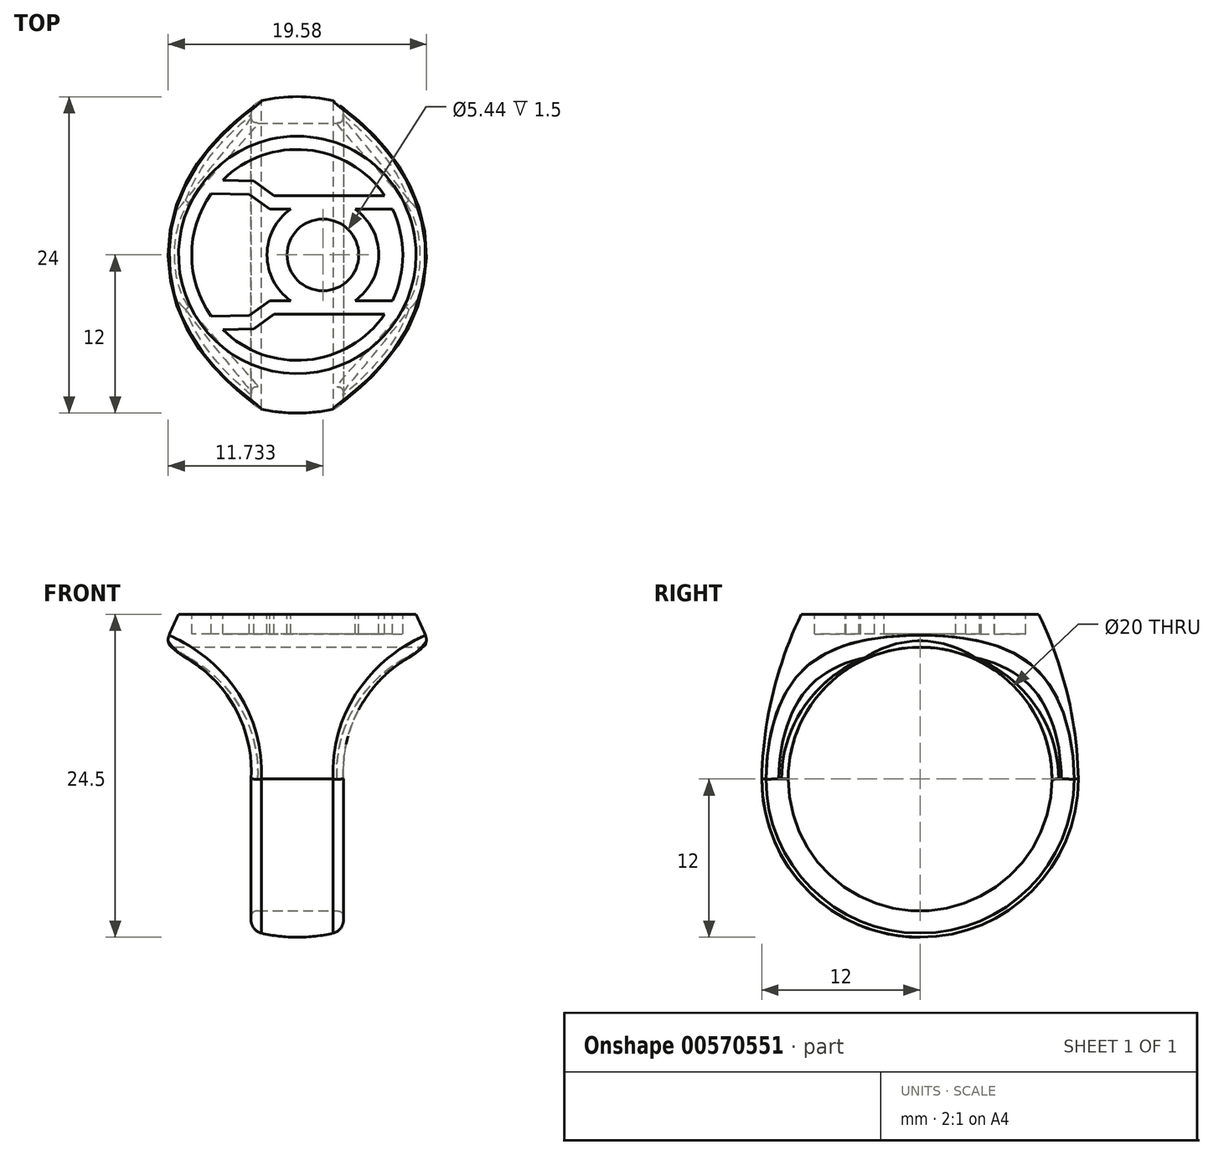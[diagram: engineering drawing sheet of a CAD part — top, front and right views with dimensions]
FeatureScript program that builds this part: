
annotation { "Feature Type Name" : "Feature", "Feature Type Description" : "" }
export const myFeature = defineFeature(function(context is Context, id is Id, definition is map)
    precondition{}
    {
        {
            var Q0;
            Q0=qCreatedBy(makeId("Right.planeOp"),FACE);
            var sketch = newSketch(context, id + "F0", { "sketchPlane" : qUnion([Q0])});
            skLineSegment(sketch, "E0", {"start": v(0, 0) * mm, "end": v(0, -24.5) * mm});
            skLineSegment(sketch, "E1", {"start": v(0, 0) * mm, "end": v(-9, 0) * mm});
            skArc(sketch, "E2", {"start": v(-12, -12.5) * mm, "mid": v(-8.49, -20.99) * mm, "end": v(0, -24.5) * mm});
            skLineSegment(sketch, "E3", {"start": v(0, -12.5) * mm, "end": v(-12, -12.5) * mm, "construction": true});
            skArc(sketch, "E4", {"start": v(-9, 0) * mm, "mid": v(-11.18, -6.09) * mm, "end": v(-12, -12.5) * mm});
            skSolve(sketch);
        }
        {
            var Q0;
            Q0=makeQuery(id+"F0.imprint","IMPRINT",FACE,{"disambiguationData":[TD([[makeQuery(id+"F0.imprint","IMPRINT",EDGE,{"derivedFrom":sQuery(id+"F0.wireOp",EDGE,"E0")}),-1.0]])]});
            var Q1;
            Q1=sQuery(id+"F0.wireOp",EDGE,"E0");
            revolve(context, id + "F1", {"entities" : qUnion([Q0]), "axis" : qUnion([Q1]), "revolveType" : RevolveType.FULL});
        }
        {
            var Q0;
            Q0=qCreatedBy(makeId("Right.planeOp"),FACE);
            var sketch = newSketch(context, id + "F2", { "sketchPlane" : qUnion([Q0])});
            skCircle(sketch, "E5", {"center": v(0, -12.5) * mm, "radius": 10 * mm});
            skSolve(sketch);
        }
        {
            var Q0;
            Q0=qSketchRegion(id+"F2",true);
            extrude(context, id + "F3", {"entities" : qUnion([Q0]), "operationType" : NewBodyOperationType.REMOVE, "oppositeDirection" : true, "depth" : 25 * mm, "offsetDistance" : 25 * mm, "symmetric" : true});
        }
        {
            var Q0;
            Q0=qCreatedBy(makeId("Front.planeOp"),FACE);
            var sketch = newSketch(context, id + "F4", { "sketchPlane" : qUnion([Q0])});
            skLineSegment(sketch, "E6", {"start": v(3.5, -26.5) * mm, "end": v(3.5, -12.5) * mm});
            skArc(sketch, "E7", {"start": v(10.15, -2.5) * mm, "mid": v(5.16, -6.39) * mm, "end": v(3.5, -12.5) * mm});
            skLineSegment(sketch, "E8", {"start": v(10.15, -2.5) * mm, "end": v(11.65, -2.5) * mm});
            skLineSegment(sketch, "E9", {"start": v(11.65, -2.5) * mm, "end": v(11.65, -26.5) * mm});
            skLineSegment(sketch, "E10", {"start": v(11.65, -26.5) * mm, "end": v(3.5, -26.5) * mm});
            skPoint(sketch, "E11.start.orphan", {"position": v(0, -24.5) * mm});
            skLineSegment(sketch, "E12", {"start": v(0, 0) * mm, "end": v(0, -24.5) * mm, "construction": true});
            skLineSegment(sketch, "E13.MirrorCS", {"start": v(-3.5, -26.5) * mm, "end": v(-3.5, -12.5) * mm});
            skArc(sketch, "E14.MirrorCS", {"start": v(-10.15, -2.5) * mm, "mid": v(-5.16, -6.39) * mm, "end": v(-3.5, -12.5) * mm});
            skLineSegment(sketch, "E15.MirrorCS", {"start": v(-11.65, -2.5) * mm, "end": v(-11.65, -26.5) * mm});
            skLineSegment(sketch, "E16.MirrorCS", {"start": v(-11.65, -26.5) * mm, "end": v(-3.5, -26.5) * mm});
            skLineSegment(sketch, "E17.MirrorCS", {"start": v(-10.15, -2.5) * mm, "end": v(-11.65, -2.5) * mm});
            skSolve(sketch);
        }
        {
            var Q0;
            Q0=qSketchRegion(id+"F4",true);
            extrude(context, id + "F5", {"entities" : qUnion([Q0]), "operationType" : NewBodyOperationType.REMOVE, "depth" : 25 * mm, "offsetDistance" : 25 * mm, "symmetric" : true});
        }
        {
            var Q0;
            Q0=makeQuery(id+"F1.opRevolve","SWEPT_FACE",FACE,{"disambiguationData":[OSD([sQuery(id+"F0.wireOp",EDGE,"E1")])]});
            var sketch = newSketch(context, id + "F6", { "sketchPlane" : qUnion([Q0])});
            skArc(sketch, "E18", {"start": v(-6.52, 4.64) * mm, "mid": v(-8, 0) * mm, "end": v(-6.52, -4.64) * mm});
            skLineSegment(sketch, "E19", {"start": v(-8, 0) * mm, "end": v(8, 0) * mm, "construction": true});
            skArc(sketch, "E20", {"start": v(4.66, 0) * mm, "mid": v(1.94, 2.72) * mm, "end": v(-0.77, 0) * mm});
            skArc(sketch, "E21", {"start": v(-0.5, 3.46) * mm, "mid": v(-1.82, 1.95) * mm, "end": v(-2.3, 0) * mm});
            skLineSegment(sketch, "E22", {"start": v(6.61, 4.5) * mm, "end": v(-1.75, 4.5) * mm});
            skLineSegment(sketch, "E23", {"start": v(-1.75, 4.5) * mm, "end": v(-3.3, 5.61) * mm});
            skLineSegment(sketch, "E24", {"start": v(-3.3, 5.61) * mm, "end": v(-5.65, 5.66) * mm});
            skLineSegment(sketch, "E25", {"start": v(7.21, 3.46) * mm, "end": v(4.38, 3.46) * mm});
            skLineSegment(sketch, "E26", {"start": v(-2.09, 3.46) * mm, "end": v(-3.64, 4.58) * mm});
            skLineSegment(sketch, "E27", {"start": v(-3.64, 4.58) * mm, "end": v(-6.52, 4.64) * mm});
            skLineSegment(sketch, "E28.trimOffspring", {"start": v(-0.5, 3.46) * mm, "end": v(-2.09, 3.46) * mm});
            skArc(sketch, "E29.trimOffspring", {"start": v(6.18, 0) * mm, "mid": v(5.7, 1.95) * mm, "end": v(4.38, 3.46) * mm});
            skArc(sketch, "E30.trimOffspring", {"start": v(6.61, 4.5) * mm, "mid": v(0.75, 7.96) * mm, "end": v(-5.65, 5.66) * mm});
            skLineSegment(sketch, "E31.MirrorCS", {"start": v(7.21, -3.46) * mm, "end": v(4.38, -3.46) * mm});
            skArc(sketch, "E32.MirrorCS", {"start": v(6.18, 0) * mm, "mid": v(5.7, -1.95) * mm, "end": v(4.38, -3.46) * mm});
            skArc(sketch, "E33.MirrorCS", {"start": v(4.66, 0) * mm, "mid": v(1.94, -2.72) * mm, "end": v(-0.77, 0) * mm});
            skArc(sketch, "E34.MirrorCS", {"start": v(-0.5, -3.46) * mm, "mid": v(-1.82, -1.95) * mm, "end": v(-2.3, 0) * mm});
            skLineSegment(sketch, "E35.MirrorCS", {"start": v(-0.5, -3.46) * mm, "end": v(-2.09, -3.46) * mm});
            skLineSegment(sketch, "E36.MirrorCS", {"start": v(6.61, -4.5) * mm, "end": v(-1.75, -4.5) * mm});
            skLineSegment(sketch, "E37.MirrorCS", {"start": v(-1.75, -4.5) * mm, "end": v(-3.3, -5.61) * mm});
            skLineSegment(sketch, "E38.MirrorCS", {"start": v(-2.09, -3.46) * mm, "end": v(-3.64, -4.58) * mm});
            skLineSegment(sketch, "E39.MirrorCS", {"start": v(-3.3, -5.61) * mm, "end": v(-5.65, -5.66) * mm});
            skLineSegment(sketch, "E40.MirrorCS", {"start": v(-3.64, -4.58) * mm, "end": v(-6.52, -4.64) * mm});
            skArc(sketch, "E41.trimOffspring", {"start": v(-5.65, -5.66) * mm, "mid": v(0.75, -7.96) * mm, "end": v(6.61, -4.5) * mm});
            skArc(sketch, "E42.trimOffspring", {"start": v(7.21, -3.46) * mm, "mid": v(8, 0) * mm, "end": v(7.21, 3.46) * mm});
            skSolve(sketch);
        }
        {
            var Q0;
            Q0=qSketchRegion(id+"F6",true);
            var Q1;
            Q1=makeQuery(id+"F6.imprint","IMPRINT",FACE,{"disambiguationData":[TD([[makeQuery(id+"F6.imprint","IMPRINT",EDGE,{"derivedFrom":sQuery(id+"F6.wireOp",EDGE,"g20j87Mm-wGr7-AMiz-bI8b-qS7GuHKO57cL")}),1.0]])]});
            extrude(context, id + "F7", {"entities" : qUnion([Q0, Q1]), "operationType" : NewBodyOperationType.REMOVE, "oppositeDirection" : true, "depth" : 1.5 * mm, "offsetDistance" : 25 * mm});
        }
        {
            var Q0;
            Q0=makeQuery(id+"F5.boolean.opBoolean","INTERSECT",EDGE,{"disambiguationData":[OD(1.0)],"derivedFrom":[makeQuery(id+"F1.opRevolve","SWEPT_FACE",FACE,{"disambiguationData":[OSD([sQuery(id+"F0.wireOp",EDGE,"E4")])]}),makeQuery(id+"F5.opExtrude","SWEPT_FACE",FACE,{"disambiguationData":[OSD([sQuery(id+"F4.wireOp",EDGE,"E14.MirrorCS")])]})]});
            var Q1;
            Q1=makeQuery(id+"F5.boolean.opBoolean","INTERSECT",EDGE,{"derivedFrom":[makeQuery(id+"F1.opRevolve","SWEPT_FACE",FACE,{"disambiguationData":[OSD([sQuery(id+"F0.wireOp",EDGE,"E2")])]}),makeQuery(id+"F5.opExtrude","SWEPT_FACE",FACE,{"disambiguationData":[OSD([sQuery(id+"F4.wireOp",EDGE,"E13.MirrorCS")])]})]});
            var Q2;
            Q2=makeQuery(id+"F5.boolean.opBoolean","INTERSECT",EDGE,{"disambiguationData":[OD(1.0)],"derivedFrom":[makeQuery(id+"F1.opRevolve","SWEPT_FACE",FACE,{"disambiguationData":[OSD([sQuery(id+"F0.wireOp",EDGE,"E4")])]}),makeQuery(id+"F5.opExtrude","SWEPT_FACE",FACE,{"disambiguationData":[OSD([sQuery(id+"F4.wireOp",EDGE,"E7")])]})]});
            var Q3;
            Q3=makeQuery(id+"F5.boolean.opBoolean","INTERSECT",EDGE,{"derivedFrom":[makeQuery(id+"F1.opRevolve","SWEPT_FACE",FACE,{"disambiguationData":[OSD([sQuery(id+"F0.wireOp",EDGE,"E2")])]}),makeQuery(id+"F5.opExtrude","SWEPT_FACE",FACE,{"disambiguationData":[OSD([sQuery(id+"F4.wireOp",EDGE,"E6")])]})]});
            fillet(context, id + "F8", {"entities" : qUnion([Q0, Q1, Q2, Q3]), "radius" : 1 * mm, "allowEdgeOverflow" : false});
        }
        {
            var Q0;
            Q0=makeQuery(id+"F5.boolean.opBoolean","INTERSECT",EDGE,{"disambiguationData":[OD(1.0)],"derivedFrom":[makeQuery(id+"F3.boolean.opBoolean","COPY",FACE,{"derivedFrom":makeQuery(id+"F3.opExtrude","SWEPT_FACE",FACE,{"disambiguationData":[OSD([sQuery(id+"F2.wireOp",EDGE,"E5")])]})}),makeQuery(id+"F5.opExtrude","SWEPT_FACE",FACE,{"disambiguationData":[OSD([sQuery(id+"F4.wireOp",EDGE,"E14.MirrorCS")])]})]});
            var Q1;
            Q1=makeQuery(id+"F5.boolean.opBoolean","INTERSECT",EDGE,{"derivedFrom":[makeQuery(id+"F3.boolean.opBoolean","COPY",FACE,{"derivedFrom":makeQuery(id+"F3.opExtrude","SWEPT_FACE",FACE,{"disambiguationData":[OSD([sQuery(id+"F2.wireOp",EDGE,"E5")])]})}),makeQuery(id+"F5.opExtrude","SWEPT_FACE",FACE,{"disambiguationData":[OSD([sQuery(id+"F4.wireOp",EDGE,"E13.MirrorCS")])]})]});
            var Q2;
            Q2=makeQuery(id+"F5.boolean.opBoolean","INTERSECT",EDGE,{"disambiguationData":[OD(0.0)],"derivedFrom":[makeQuery(id+"F3.boolean.opBoolean","COPY",FACE,{"derivedFrom":makeQuery(id+"F3.opExtrude","SWEPT_FACE",FACE,{"disambiguationData":[OSD([sQuery(id+"F2.wireOp",EDGE,"E5")])]})}),makeQuery(id+"F5.opExtrude","SWEPT_FACE",FACE,{"disambiguationData":[OSD([sQuery(id+"F4.wireOp",EDGE,"E14.MirrorCS")])]})]});
            var Q3;
            Q3=makeQuery(id+"F5.boolean.opBoolean","INTERSECT",EDGE,{"disambiguationData":[OD(0.0)],"derivedFrom":[makeQuery(id+"F3.boolean.opBoolean","COPY",FACE,{"derivedFrom":makeQuery(id+"F3.opExtrude","SWEPT_FACE",FACE,{"disambiguationData":[OSD([sQuery(id+"F2.wireOp",EDGE,"E5")])]})}),makeQuery(id+"F5.opExtrude","SWEPT_FACE",FACE,{"disambiguationData":[OSD([sQuery(id+"F4.wireOp",EDGE,"E7")])]})]});
            var Q4;
            Q4=makeQuery(id+"F3.boolean.opBoolean","COPY",FACE,{"derivedFrom":makeQuery(id+"F3.opExtrude","SWEPT_FACE",FACE,{"disambiguationData":[OSD([sQuery(id+"F2.wireOp",EDGE,"E5")])]})});
            fillet(context, id + "F9", {"entities" : qUnion([Q0, Q1, Q2, Q3, Q4]), "radius" : .5 * mm, "rho" : 0.5, "crossSection" : FilletCrossSection.CONIC, "allowEdgeOverflow" : false});
        }
    });
